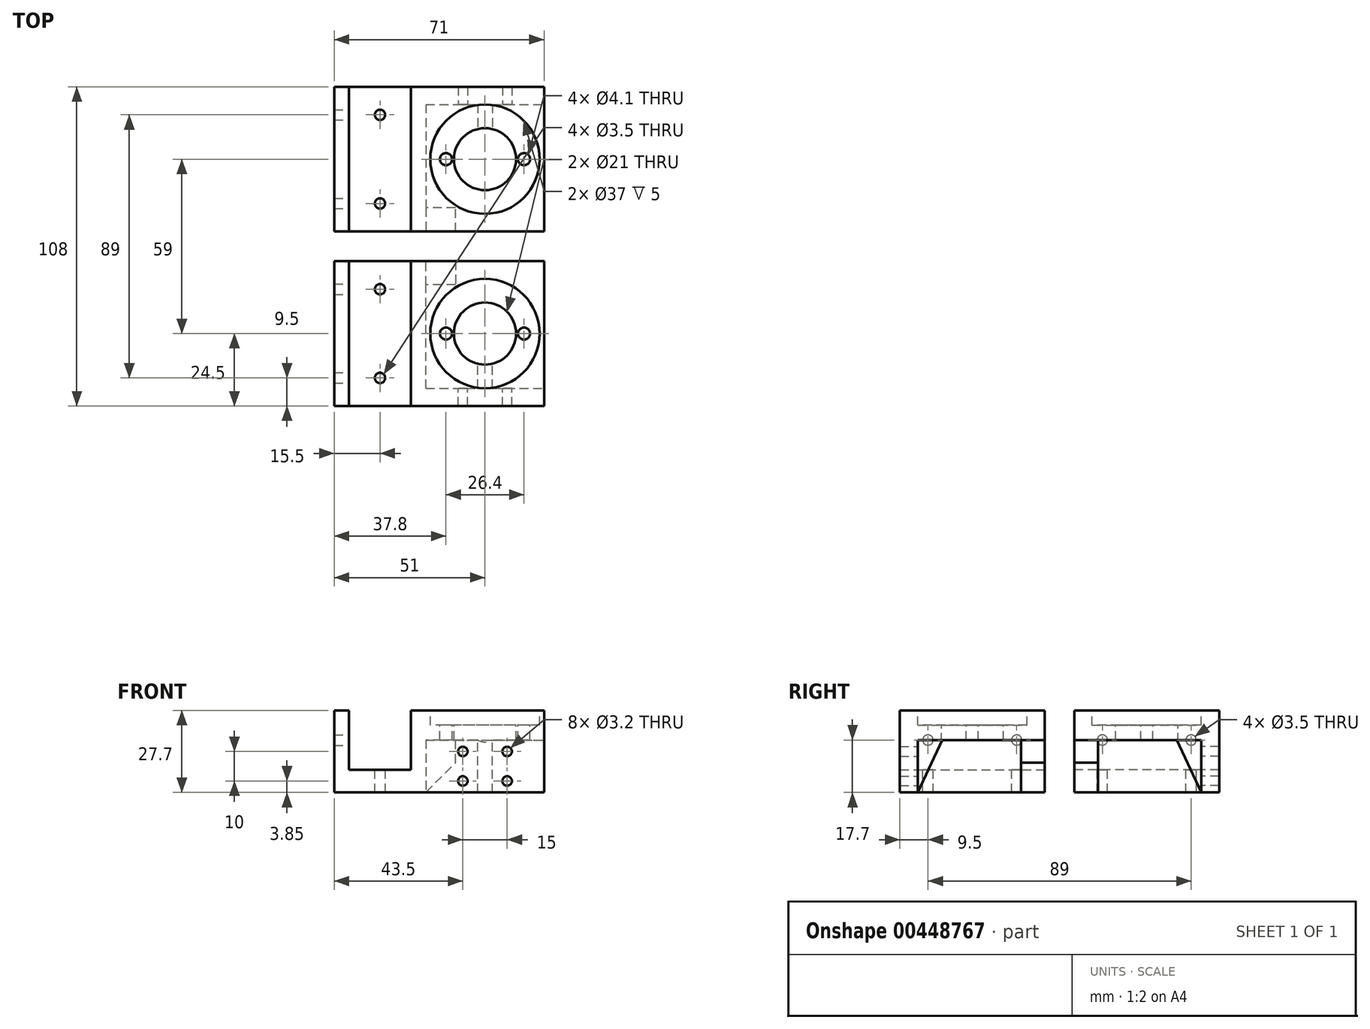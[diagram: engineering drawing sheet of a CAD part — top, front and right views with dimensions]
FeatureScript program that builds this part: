
annotation { "Feature Type Name" : "Feature", "Feature Type Description" : "" }
export const myFeature = defineFeature(function(context is Context, id is Id, definition is map)
    precondition{}
    {
        {
            var Q0;
            Q0=qCreatedBy(makeId("Front.planeOp"),FACE);
            var sketch = newSketch(context, id + "F0", { "sketchPlane" : qUnion([Q0])});
            skLineSegment(sketch, "E0.bottom", {"start": v(0, 0) * mm, "end": v(27, 0) * mm, "construction": true});
            skLineSegment(sketch, "E0.top", {"start": v(0, 27.7) * mm, "end": v(27, 27.7) * mm, "construction": true});
            skLineSegment(sketch, "E0.left", {"start": v(0, 0) * mm, "end": v(0, 27.7) * mm, "construction": true});
            skLineSegment(sketch, "E0.right", {"start": v(27, 0) * mm, "end": v(27, 27.7) * mm, "construction": true});
            skLineSegment(sketch, "E1.bottom", {"start": v(-6.5, 27.7) * mm, "end": v(33.5, 27.7) * mm});
            skLineSegment(sketch, "E1.top", {"start": v(-6.5, 0) * mm, "end": v(33.5, 0) * mm});
            skLineSegment(sketch, "E1.left", {"start": v(-6.5, 27.7) * mm, "end": v(-6.5, 0) * mm});
            skLineSegment(sketch, "E1.right", {"start": v(33.5, 27.7) * mm, "end": v(33.5, 0) * mm});
            skSolve(sketch);
        }
        {
            var Q0;
            Q0=makeQuery(id+"F0.imprint","IMPRINT",FACE,{"disambiguationData":[TD([[makeQuery(id+"F0.imprint","IMPRINT",EDGE,{"derivedFrom":sQuery(id+"F0.wireOp",EDGE,"E0.bottom")}),1.0]])]});
            var Q1;
            Q1=makeQuery(id+"F0.imprint","IMPRINT",FACE,{"disambiguationData":[TD([[makeQuery(id+"F0.imprint","IMPRINT",EDGE,{"derivedFrom":sQuery(id+"F0.wireOp",EDGE,"E1.bottom")}),-1.0]])]});
            extrude(context, id + "F1", {"entities" : qUnion([Q0, Q1]), "depth" : 6 * mm});
        }
        {
            var Q0;
            Q0=makeQuery(id+"F1.opExtrude","CAP_FACE",FACE,{"disambiguationData":[OSD([sQuery(id+"F0.wireOp",EDGE,"E1.bottom"),sQuery(id+"F0.wireOp",EDGE,"E1.top"),sQuery(id+"F0.wireOp",EDGE,"E1.left"),sQuery(id+"F0.wireOp",EDGE,"E1.right")])],"isStart":false});
            var sketch = newSketch(context, id + "F2", { "sketchPlane" : qUnion([Q0])});
            skLineSegment(sketch, "E2.bottom", {"start": v(-6.5, 27.7) * mm, "end": v(33.5, 27.7) * mm});
            skLineSegment(sketch, "E2.top", {"start": v(-6.5, 17.7) * mm, "end": v(33.5, 17.7) * mm});
            skLineSegment(sketch, "E2.left", {"start": v(-6.5, 27.7) * mm, "end": v(-6.5, 17.7) * mm});
            skLineSegment(sketch, "E2.right", {"start": v(33.5, 27.7) * mm, "end": v(33.5, 17.7) * mm});
            skLineSegment(sketch, "E3", {"start": v(13.5, 27.7) * mm, "end": v(13.5, 0) * mm, "construction": true});
            skSolve(sketch);
        }
        {
            var Q0;
            Q0=makeQuery(id+"F2.imprint","IMPRINT",FACE,{"disambiguationData":[TD([[makeQuery(id+"F2.imprint","IMPRINT",EDGE,{"derivedFrom":sQuery(id+"F2.wireOp",EDGE,"E2.bottom")}),-1.0]])]});
            extrude(context, id + "F3", {"entities" : qUnion([Q0]), "operationType" : NewBodyOperationType.ADD, "depth" : 43 * mm});
        }
        {
            var Q0;
            Q0=makeQuery(id+"F3.opExtrude","SWEPT_FACE",FACE,{"disambiguationData":[OSD([sQuery(id+"F2.wireOp",EDGE,"E2.bottom")])]});
            var sketch = newSketch(context, id + "F4", { "sketchPlane" : qUnion([Q0])});
            skCircle(sketch, "E4", {"center": v(13.5, -24.5) * mm, "radius": 18.5 * mm});
            skPoint(sketch, "E4.centerSnap0", {"position": v(13.5, -3) * mm});
            skPoint(sketch, "E4.centerSnap1", {"position": v(-6.5, -24.5) * mm});
            skSolve(sketch);
        }
        {
            var Q0;
            Q0=makeQuery(id+"F4.imprint","IMPRINT",FACE,{"disambiguationData":[TD([[makeQuery(id+"F4.imprint","IMPRINT",EDGE,{"derivedFrom":sQuery(id+"F4.wireOp",EDGE,"E4")}),1.0]])]});
            extrude(context, id + "F5", {"entities" : qUnion([Q0]), "operationType" : NewBodyOperationType.REMOVE, "oppositeDirection" : true, "depth" : 5 * mm});
        }
        {
            var Q0;
            Q0=makeQuery(id+"F5.boolean.opBoolean","COPY",FACE,{"derivedFrom":makeQuery(id+"F5.opExtrude","CAP_FACE",FACE,{"disambiguationData":[OSD([sQuery(id+"F4.wireOp",EDGE,"E4")])],"isStart":false})});
            var sketch = newSketch(context, id + "F6", { "sketchPlane" : qUnion([Q0])});
            skCircle(sketch, "E5", {"center": v(13.5, -24.5) * mm, "radius": 10.5 * mm});
            skLineSegment(sketch, "E6", {"start": v(13.5, -24.5) * mm, "end": v(32, -24.5) * mm, "construction": true});
            skLineSegment(sketch, "E7", {"start": v(13.5, -24.5) * mm, "end": v(-5, -24.5) * mm, "construction": true});
            skCircle(sketch, "E8", {"center": v(13.5, -24.5) * mm, "radius": 13.2 * mm, "construction": true});
            skCircle(sketch, "E9", {"center": v(26.7, -24.5) * mm, "radius": 2.05 * mm});
            skCircle(sketch, "E10", {"center": v(0.3, -24.5) * mm, "radius": 2.05 * mm});
            skSolve(sketch);
        }
        {
            var Q0;
            Q0=qSketchRegion(id+"F6",true);
            extrude(context, id + "F7", {"entities" : qUnion([Q0]), "operationType" : NewBodyOperationType.REMOVE, "endBound" : BoundingType.THROUGH_ALL, "oppositeDirection" : true, "depth" : 25 * mm});
        }
        {
            var Q0;
            Q0=makeQuery(id+"F3.boolean.opBoolean","MERGE",FACE,{"derivedFrom":[makeQuery(id+"F1.opExtrude","SWEPT_FACE",FACE,{"disambiguationData":[OSD([sQuery(id+"F0.wireOp",EDGE,"E1.left")])]}),makeQuery(id+"F3.opExtrude","SWEPT_FACE",FACE,{"disambiguationData":[OSD([sQuery(id+"F2.wireOp",EDGE,"E2.left")])]})]});
            var sketch = newSketch(context, id + "F8", { "sketchPlane" : qUnion([Q0])});
            skLineSegment(sketch, "E11.bottom", {"start": v(0, 0) * mm, "end": v(49, 0) * mm});
            skLineSegment(sketch, "E11.top", {"start": v(0, 27.7) * mm, "end": v(49, 27.7) * mm});
            skLineSegment(sketch, "E11.left", {"start": v(0, 0) * mm, "end": v(0, 27.7) * mm});
            skLineSegment(sketch, "E11.right", {"start": v(49, 0) * mm, "end": v(49, 27.7) * mm});
            skSolve(sketch);
        }
        {
            var Q0;
            {var subQ1=sQuery(id+"F2.wireOp",EDGE,"E2.top");var subQ2=sQuery(id+"F2.wireOp",EDGE,"E2.left");var subQ3=sQuery(id+"F0.wireOp",EDGE,"E1.left");var subQ8=makeQuery(id+"F3.opExtrude","SWEPT_EDGE",EDGE,{"disambiguationData":[OSD([subQ3,subQ1,subQ2])]});Q0=makeQuery(id+"F8.imprint","IMPRINT",FACE,{"disambiguationData":[TD([[makeQuery(id+"F8.imprint","IMPRINT",EDGE,{"derivedFrom":subQ8}),1.0]])]});}
            var Q1;
            {var subQ12=sQuery(id+"F8.wireOp",EDGE,"E11.left");Q1=makeQuery(id+"F8.imprint","IMPRINT",FACE,{"disambiguationData":[TD([[makeQuery(id+"F8.imprint","IMPRINT",EDGE,{"derivedFrom":subQ12}),1.0]])]});}
            extrude(context, id + "F9", {"entities" : qUnion([Q0, Q1]), "operationType" : NewBodyOperationType.ADD, "depth" : 31 * mm});
        }
        {
            var Q0;
            Q0=makeQuery(id+"F9.boolean.opBoolean","MERGE",FACE,{"derivedFrom":[makeQuery(id+"F3.opExtrude","CAP_FACE",FACE,{"disambiguationData":[OSD([sQuery(id+"F2.wireOp",EDGE,"E2.bottom"),sQuery(id+"F2.wireOp",EDGE,"E2.top"),sQuery(id+"F2.wireOp",EDGE,"E2.left"),sQuery(id+"F2.wireOp",EDGE,"E2.right")])],"isStart":false}),makeQuery(id+"F9.opExtrude","SWEPT_FACE",FACE,{"disambiguationData":[OSD([sQuery(id+"F8.wireOp",EDGE,"E11.right")])]})]});
            var sketch = newSketch(context, id + "F10", { "sketchPlane" : qUnion([Q0])});
            skLineSegment(sketch, "E12", {"start": v(-32.5, 27.7) * mm, "end": v(-32.5, 7.7) * mm});
            skLineSegment(sketch, "E13", {"start": v(-32.5, 7.7) * mm, "end": v(-11.5, 7.7) * mm});
            skLineSegment(sketch, "E14", {"start": v(-11.5, 7.7) * mm, "end": v(-11.5, 27.7) * mm});
            skLineSegment(sketch, "E15", {"start": v(-32.5, 27.7) * mm, "end": v(-11.5, 27.7) * mm});
            skSolve(sketch);
        }
        {
            var Q0;
            Q0=makeQuery(id+"F10.imprint","IMPRINT",FACE,{"disambiguationData":[TD([[makeQuery(id+"F10.imprint","IMPRINT",EDGE,{"derivedFrom":sQuery(id+"F10.wireOp",EDGE,"E12")}),1.0]])]});
            extrude(context, id + "F11", {"entities" : qUnion([Q0]), "operationType" : NewBodyOperationType.REMOVE, "endBound" : BoundingType.THROUGH_ALL, "oppositeDirection" : true, "depth" : 25 * mm});
        }
        {
            var Q0;
            Q0=makeQuery(id+"F3.opExtrude","SWEPT_FACE",FACE,{"disambiguationData":[OSD([sQuery(id+"F2.wireOp",EDGE,"E2.top")])]});
            var sketch = newSketch(context, id + "F12", { "sketchPlane" : qUnion([Q0])});
            skLineSegment(sketch, "E16.bottom", {"start": v(11, 6) * mm, "end": v(16, 6) * mm});
            skLineSegment(sketch, "E16.left", {"start": v(11, 6) * mm, "end": v(11, 14.3) * mm});
            skLineSegment(sketch, "E16.right", {"start": v(16, 6) * mm, "end": v(16, 14.3) * mm});
            skArc(sketch, "E17", {"start": v(16, 14.3) * mm, "mid": v(13.5, 14) * mm, "end": v(11, 14.3) * mm});
            skPoint(sketch, "E18", {"position": v(13.5, 6) * mm});
            skSolve(sketch);
        }
        {
            var Q0;
            Q0=makeQuery(id+"F12.imprint","IMPRINT",FACE,{"disambiguationData":[TD([[makeQuery(id+"F12.imprint","IMPRINT",EDGE,{"derivedFrom":sQuery(id+"F12.wireOp",EDGE,"E16.bottom")}),1.0]])]});
            var Q1;
            Q1=makeQuery(id+"F9.boolean.opBoolean","MERGE",FACE,{"derivedFrom":[makeQuery(id+"F1.opExtrude","SWEPT_FACE",FACE,{"disambiguationData":[OSD([sQuery(id+"F0.wireOp",EDGE,"E1.top")])]}),makeQuery(id+"F9.opExtrude","SWEPT_FACE",FACE,{"disambiguationData":[OSD([sQuery(id+"F8.wireOp",EDGE,"E11.bottom")])]})]});
            extrude(context, id + "F13", {"entities" : qUnion([Q0]), "operationType" : NewBodyOperationType.ADD, "endBound" : BoundingType.UP_TO_SURFACE, "endBoundEntityFace" : qUnion([Q1]), "depth" : 25 * mm});
        }
        {
            var Q0;
            Q0=makeQuery(id+"F13.opExtrude","SWEPT_FACE",FACE,{"disambiguationData":[OSD([sQuery(id+"F12.wireOp",EDGE,"E16.right")])]});
            var sketch = newSketch(context, id + "F14", { "sketchPlane" : qUnion([Q0])});
            skLineSegment(sketch, "E19", {"start": v(-14.3, 17.7) * mm, "end": v(-6, 0) * mm});
            skLineSegment(sketch, "E20", {"start": v(-6, 0) * mm, "end": v(-6, 17.7) * mm});
            skLineSegment(sketch, "E21", {"start": v(-6, 17.7) * mm, "end": v(-14.3, 17.7) * mm});
            skSolve(sketch);
        }
        {
            var Q0;
            Q0=makeQuery(id+"F14.imprint","IMPRINT",FACE,{"disambiguationData":[TD([[makeQuery(id+"F14.imprint","IMPRINT",EDGE,{"derivedFrom":sQuery(id+"F14.wireOp",EDGE,"E19")}),-1.0]])]});
            var Q1;
            Q1=makeQuery(id+"F13.opExtrude","SWEPT_FACE",FACE,{"disambiguationData":[OSD([sQuery(id+"F12.wireOp",EDGE,"E16.left")])]});
            extrude(context, id + "F15", {"entities" : qUnion([Q0]), "operationType" : NewBodyOperationType.REMOVE, "endBound" : BoundingType.UP_TO_SURFACE, "oppositeDirection" : true, "endBoundEntityFace" : qUnion([Q1]), "depth" : 25 * mm});
        }
        {
            var Q0;
            Q0=makeQuery(id+"F9.opExtrude","CAP_FACE",FACE,{"disambiguationData":[OSD([sQuery(id+"F8.wireOp",EDGE,"E11.bottom"),sQuery(id+"F8.wireOp",EDGE,"E11.top"),sQuery(id+"F8.wireOp",EDGE,"E11.left"),sQuery(id+"F8.wireOp",EDGE,"E11.right")])],"isStart":true});
            var sketch = newSketch(context, id + "F16", { "sketchPlane" : qUnion([Q0])});
            skLineSegment(sketch, "E22.bottom", {"start": v(-49, 17.7) * mm, "end": v(-41, 17.7) * mm});
            skLineSegment(sketch, "E22.top", {"start": v(-49, 0) * mm, "end": v(-41, 0) * mm});
            skLineSegment(sketch, "E22.left", {"start": v(-49, 17.7) * mm, "end": v(-49, 0) * mm});
            skLineSegment(sketch, "E22.right", {"start": v(-41, 17.7) * mm, "end": v(-41, 0) * mm});
            skSolve(sketch);
        }
        {
            var Q0;
            Q0=makeQuery(id+"F16.imprint","IMPRINT",FACE,{"disambiguationData":[TD([[makeQuery(id+"F16.imprint","IMPRINT",EDGE,{"derivedFrom":sQuery(id+"F16.wireOp",EDGE,"E22.bottom")}),-1.0]])]});
            var Q1;
            Q1=makeQuery(id+"F16.imprint","IMPRINT",FACE,{"disambiguationData":[TD([[makeQuery(id+"F16.imprint","IMPRINT",EDGE,{"derivedFrom":sQuery(id+"F16.wireOp",EDGE,"8BEWw2aY-geet-BJQ8-Mbal-S3a0Wca1nJoR.bottom")}),-1.0]])]});
            extrude(context, id + "F17", {"entities" : qUnion([Q0, Q1]), "operationType" : NewBodyOperationType.ADD, "depth" : 10 * mm});
        }
        {
            var Q0;
            Q0=makeQuery(id+"F11.boolean.opBoolean","COPY",FACE,{"derivedFrom":makeQuery(id+"F11.opExtrude","SWEPT_FACE",FACE,{"disambiguationData":[OSD([sQuery(id+"F10.wireOp",EDGE,"E13")])]})});
            var sketch = newSketch(context, id + "F18", { "sketchPlane" : qUnion([Q0])});
            skLineSegment(sketch, "E23", {"start": v(-22, 0) * mm, "end": v(-22, -49) * mm, "construction": true});
            skCircle(sketch, "E24", {"center": v(-22, -9.5) * mm, "radius": 1.75 * mm});
            skCircle(sketch, "E25", {"center": v(-22, -39.5) * mm, "radius": 1.75 * mm});
            skSolve(sketch);
        }
        {
            var Q0;
            Q0=makeQuery(id+"F18.imprint","IMPRINT",FACE,{"disambiguationData":[TD([[makeQuery(id+"F18.imprint","IMPRINT",EDGE,{"derivedFrom":sQuery(id+"F18.wireOp",EDGE,"E25")}),1.0]])]});
            var Q1;
            Q1=makeQuery(id+"F18.imprint","IMPRINT",FACE,{"disambiguationData":[TD([[makeQuery(id+"F18.imprint","IMPRINT",EDGE,{"derivedFrom":sQuery(id+"F18.wireOp",EDGE,"E24")}),1.0]])]});
            extrude(context, id + "F19", {"entities" : qUnion([Q0, Q1]), "operationType" : NewBodyOperationType.REMOVE, "endBound" : BoundingType.THROUGH_ALL, "oppositeDirection" : true, "depth" : 25 * mm});
        }
        {
            var Q0;
            Q0=makeQuery(id+"F11.boolean.opBoolean","COPY",FACE,{"derivedFrom":makeQuery(id+"F11.opExtrude","SWEPT_FACE",FACE,{"disambiguationData":[OSD([sQuery(id+"F10.wireOp",EDGE,"E12")])]})});
            var sketch = newSketch(context, id + "F20", { "sketchPlane" : qUnion([Q0])});
            skLineSegment(sketch, "E26", {"start": v(-49, 17.7) * mm, "end": v(0, 17.7) * mm, "construction": true});
            skCircle(sketch, "E27", {"center": v(-39.5, 17.7) * mm, "radius": 1.75 * mm});
            skCircle(sketch, "E28", {"center": v(-9.5, 17.7) * mm, "radius": 1.75 * mm});
            skSolve(sketch);
        }
        {
            var Q0;
            Q0=makeQuery(id+"F20.imprint","IMPRINT",FACE,{"disambiguationData":[TD([[makeQuery(id+"F20.imprint","IMPRINT",EDGE,{"derivedFrom":sQuery(id+"F20.wireOp",EDGE,"E27")}),1.0]])]});
            var Q1;
            Q1=makeQuery(id+"F20.imprint","IMPRINT",FACE,{"disambiguationData":[TD([[makeQuery(id+"F20.imprint","IMPRINT",EDGE,{"derivedFrom":sQuery(id+"F20.wireOp",EDGE,"E28")}),1.0]])]});
            extrude(context, id + "F21", {"entities" : qUnion([Q0, Q1]), "operationType" : NewBodyOperationType.REMOVE, "endBound" : BoundingType.THROUGH_ALL, "oppositeDirection" : true, "depth" : 25 * mm});
        }
        {
            var Q0;
            {var subQ2=sQuery(id+"F0.wireOp",EDGE,"E1.top");var subQ3=makeQuery(id+"F1.opExtrude","SWEPT_FACE",FACE,{"disambiguationData":[OSD([subQ2])]});var subQ4=sQuery(id+"F0.wireOp",EDGE,"E1.right");var subQ5=sQuery(id+"F0.wireOp",EDGE,"E1.left");Q0=makeQuery(id+"F13.boolean.opBoolean","SPLIT",FACE,{"disambiguationData":[TD([makeQuery(id+"F13.opExtrude","SWEPT_FACE",FACE,{"disambiguationData":[OSD([sQuery(id+"F12.wireOp",EDGE,"E16.left")])]})])],"derivedFrom":makeQuery(id+"F3.boolean.opBoolean","SPLIT",FACE,{"disambiguationData":[TD([subQ3])],"derivedFrom":makeQuery(id+"F1.opExtrude","CAP_FACE",FACE,{"disambiguationData":[OSD([sQuery(id+"F0.wireOp",EDGE,"E1.bottom"),subQ2,subQ5,subQ4])],"isStart":false})})});}
            var sketch = newSketch(context, id + "F22", { "sketchPlane" : qUnion([Q0])});
            skLineSegment(sketch, "E29.bottom", {"start": v(6, 13.85) * mm, "end": v(21, 13.85) * mm, "construction": true});
            skLineSegment(sketch, "E29.top", {"start": v(6, 3.85) * mm, "end": v(21, 3.85) * mm, "construction": true});
            skLineSegment(sketch, "E29.left", {"start": v(6, 13.85) * mm, "end": v(6, 3.85) * mm, "construction": true});
            skLineSegment(sketch, "E29.right", {"start": v(21, 13.85) * mm, "end": v(21, 3.85) * mm, "construction": true});
            skPoint(sketch, "E30", {"position": v(6, 8.85) * mm});
            skPoint(sketch, "E31", {"position": v(13.5, 13.85) * mm});
            skPoint(sketch, "E32", {"position": v(11, 8.85) * mm});
            skSolve(sketch);
        }
        {
            var Q0;
            Q0=sQuery(id+"F22.wireOp",VERTEX,"E29.left.end");
            var Q1;
            Q1=sQuery(id+"F22.wireOp",VERTEX,"E29.left.start");
            var Q2;
            Q2=sQuery(id+"F22.wireOp",VERTEX,"E29.right.start");
            var Q3;
            Q3=sQuery(id+"F22.wireOp",VERTEX,"E29.right.end");
            var Q4;
            Q4=makeQuery(id+"F1.opExtrude","SWEPT_BODY",BODY,{"disambiguationData":[OSD([sQuery(id+"F0.wireOp",EDGE,"E1.bottom"),sQuery(id+"F0.wireOp",EDGE,"E1.top"),sQuery(id+"F0.wireOp",EDGE,"E1.left"),sQuery(id+"F0.wireOp",EDGE,"E1.right")])]});
            hole(context, id + "F23", {"style" : HoleStyle.SIMPLE, "endStyle" : HoleEndStyle.THROUGH, "holeDiameter" : 3.2 * mm, "locations" : qUnion([Q0, Q1, Q2, Q3]), "scope" : qUnion([Q4]), "isTappedThrough" : true});
        }
        {
            var Q0;
            Q0=makeQuery(id+"F17.opExtrude","CAP_EDGE",EDGE,{"disambiguationData":[OSD([sQuery(id+"F16.wireOp",EDGE,"E22.top")])],"isStart":false});
            chamfer(context, id + "F24", {"entities" : qUnion([Q0]), "width" : 10 * mm, "tangentPropagation" : true});
        }
        {
            var Q0;
            Q0=makeQuery(id+"F17.boolean.opBoolean","MERGE",FACE,{"derivedFrom":[makeQuery(id+"F9.boolean.opBoolean","MERGE",FACE,{"derivedFrom":[makeQuery(id+"F3.opExtrude","CAP_FACE",FACE,{"disambiguationData":[OSD([sQuery(id+"F2.wireOp",EDGE,"E2.bottom"),sQuery(id+"F2.wireOp",EDGE,"E2.top"),sQuery(id+"F2.wireOp",EDGE,"E2.left"),sQuery(id+"F2.wireOp",EDGE,"E2.right")])],"isStart":false}),makeQuery(id+"F9.opExtrude","SWEPT_FACE",FACE,{"disambiguationData":[OSD([sQuery(id+"F8.wireOp",EDGE,"E11.right")])]})]}),makeQuery(id+"F17.opExtrude","SWEPT_FACE",FACE,{"disambiguationData":[OSD([sQuery(id+"F16.wireOp",EDGE,"E22.left")])]})]});
            cPlane(context, id + "F25", {"entities" : qUnion([Q0]), "cplaneType" : CPlaneType.OFFSET, "offset" : 5 * mm, "width" : 150 * mm, "height" : 150 * mm});
        }
        {
            var Q0;
            Q0=makeQuery(id+"F1.opExtrude","SWEPT_BODY",BODY,{"disambiguationData":[OSD([sQuery(id+"F0.wireOp",EDGE,"E1.bottom"),sQuery(id+"F0.wireOp",EDGE,"E1.top"),sQuery(id+"F0.wireOp",EDGE,"E1.left"),sQuery(id+"F0.wireOp",EDGE,"E1.right")])]});
            var Q1;
            Q1=qCreatedBy(id+"F25.planeOp",FACE);
            mirror(context, id + "F26", {"entities" : qUnion([Q0]), "mirrorPlane" : qUnion([Q1])});
        }
    });
